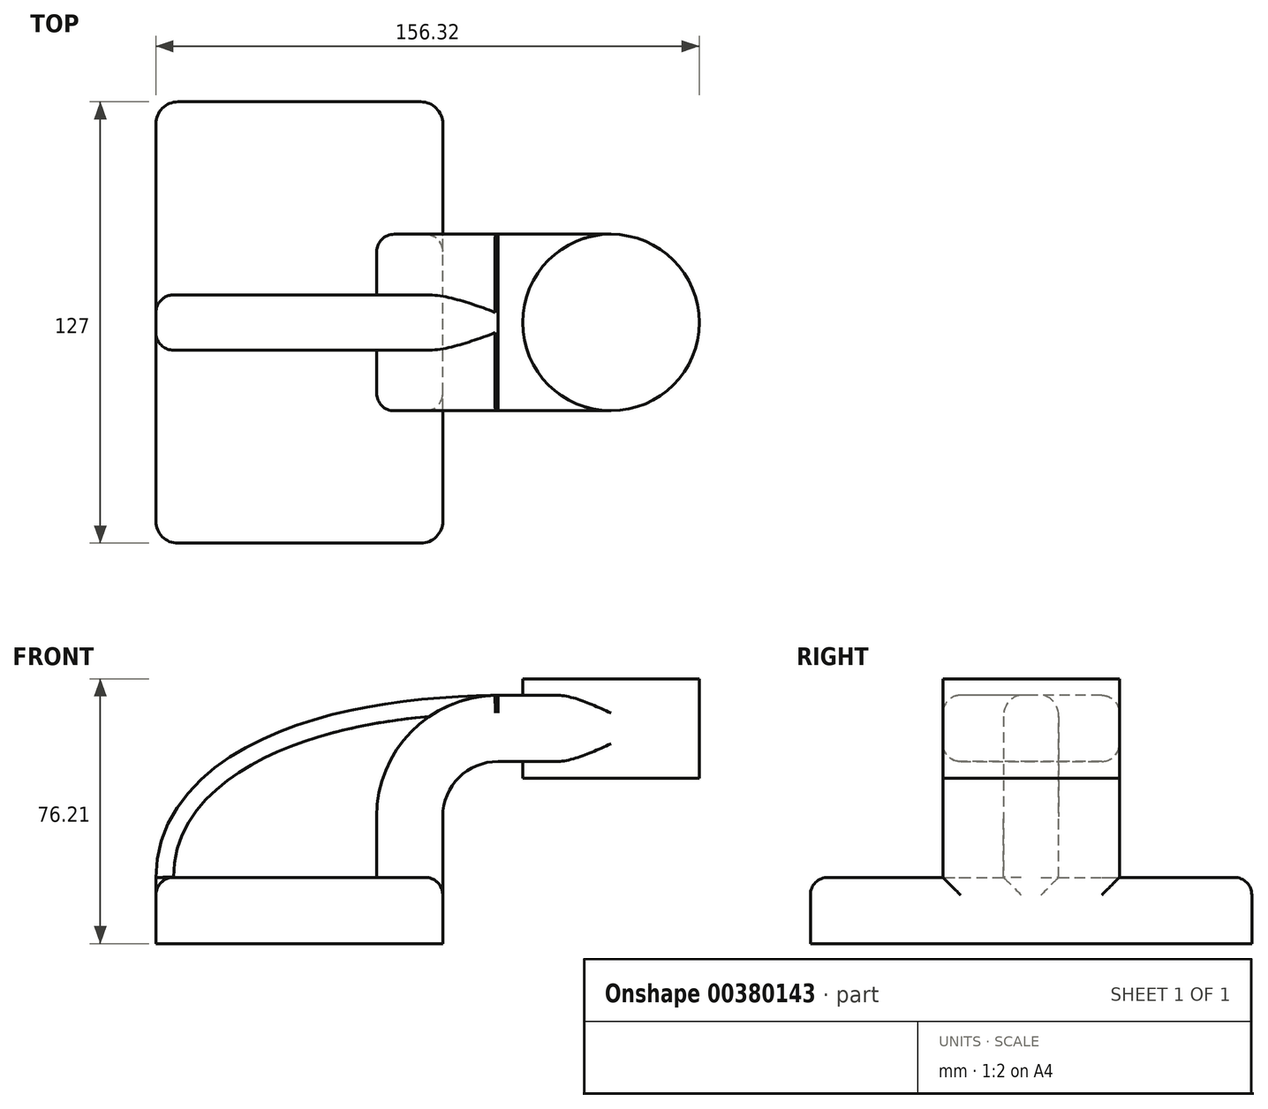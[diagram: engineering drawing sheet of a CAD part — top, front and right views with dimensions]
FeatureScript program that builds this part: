
annotation { "Feature Type Name" : "Feature", "Feature Type Description" : "" }
export const myFeature = defineFeature(function(context is Context, id is Id, definition is map)
    precondition{}
    {
        {
            var Q0;
            Q0=qCreatedBy(makeId("Front.planeOp"),FACE);
            var sketch = newSketch(context, id + "F0", { "sketchPlane" : qUnion([Q0])});
            skLineSegment(sketch, "E0.bottom", {"start": v(41.28, -9.52) * mm, "end": v(-41.28, -9.53) * mm});
            skLineSegment(sketch, "E0.top", {"start": v(41.27, 9.53) * mm, "end": v(-41.28, 9.53) * mm});
            skLineSegment(sketch, "E0.left", {"start": v(41.28, -9.52) * mm, "end": v(41.28, 9.53) * mm});
            skLineSegment(sketch, "E0.right", {"start": v(-41.28, -9.52) * mm, "end": v(-41.28, 9.53) * mm});
            skPoint(sketch, "E0.middle", {"position": v(0, 0) * mm});
            skLineSegment(sketch, "E1.bottom", {"start": v(115.04, 38.1) * mm, "end": v(64.24, 38.1) * mm});
            skLineSegment(sketch, "E1.top", {"start": v(115.04, 66.68) * mm, "end": v(64.24, 66.68) * mm});
            skLineSegment(sketch, "E1.left", {"start": v(115.04, 38.1) * mm, "end": v(115.04, 66.68) * mm});
            skLineSegment(sketch, "E1.right", {"start": v(64.24, 38.1) * mm, "end": v(64.24, 66.68) * mm});
            skPoint(sketch, "E1.middle", {"position": v(89.64, 52.39) * mm});
            skLineSegment(sketch, "E2", {"start": v(41.27, 9.53) * mm, "end": v(41.27, 27) * mm});
            skArc(sketch, "E3", {"start": v(41.27, 27) * mm, "mid": v(45.92, 38.23) * mm, "end": v(57.15, 42.88) * mm});
            skLineSegment(sketch, "E4", {"start": v(57.15, 42.88) * mm, "end": v(80.73, 42.88) * mm});
            skLineSegment(sketch, "E5.0", {"start": v(57.15, 61.93) * mm, "end": v(89.64, 61.93) * mm});
            skArc(sketch, "E5.1", {"start": v(22.23, 27) * mm, "mid": v(32.45, 51.7) * mm, "end": v(57.15, 61.93) * mm});
            skLineSegment(sketch, "E5.2", {"start": v(22.22, 9.53) * mm, "end": v(22.22, 27) * mm});
            skLineSegment(sketch, "E6", {"start": v(89.64, 38.1) * mm, "end": v(89.64, 66.68) * mm});
            skLineSegment(sketch, "E7", {"start": v(80.73, 42.88) * mm, "end": v(89.64, 42.88) * mm});
            skFitSpline(sketch, "E8", {"points": [v(-41.28, 9.53) * mm, v(57.15, 61.93) * mm], "startDerivative": vector(-0.8, 82.6) * mm, "endDerivative": vector(200.95, 2.16) * mm});
            skSolve(sketch);
        }
        {
            var Q0;
            Q0=makeQuery(id+"F0.imprint","IMPRINT",FACE,{"disambiguationData":[TD([[makeQuery(id+"F0.imprint","IMPRINT",EDGE,{"derivedFrom":sQuery(id+"F0.wireOp",EDGE,"E0.bottom")}),-1.0]])]});
            extrude(context, id + "F1", {"entities" : qUnion([Q0]), "endBound" : BoundingType.SYMMETRIC, "depth" : 127 * mm});
        }
        {
            var Q0;
            {var subQ1=sQuery(id+"F0.wireOp",EDGE,"E2");Q0=makeQuery(id+"F0.imprint","IMPRINT",FACE,{"disambiguationData":[TD([[makeQuery(id+"F0.imprint","IMPRINT",EDGE,{"derivedFrom":subQ1}),1.0]])]});}
            var Q1;
            {var subQ3=sQuery(id+"F0.wireOp",EDGE,"E7");Q1=makeQuery(id+"F0.imprint","IMPRINT",FACE,{"disambiguationData":[TD([[makeQuery(id+"F0.imprint","IMPRINT",EDGE,{"derivedFrom":subQ3}),1.0]])]});}
            extrude(context, id + "F2", {"entities" : qUnion([Q0, Q1]), "operationType" : NewBodyOperationType.ADD, "endBound" : BoundingType.SYMMETRIC, "depth" : 50.8 * mm});
        }
        {
            var Q0;
            {var subQ3=sQuery(id+"F0.wireOp",EDGE,"E5.2");Q0=makeQuery(id+"F0.imprint","IMPRINT",FACE,{"disambiguationData":[TD([[makeQuery(id+"F0.imprint","IMPRINT",EDGE,{"derivedFrom":subQ3}),1.0]])]});}
            extrude(context, id + "F3", {"entities" : qUnion([Q0]), "operationType" : NewBodyOperationType.ADD, "endBound" : BoundingType.SYMMETRIC, "depth" : 15.88 * mm});
        }
        {
            var Q0;
            {var subQ0=sQuery(id+"F0.wireOp",EDGE,"E1.left");Q0=makeQuery(id+"F0.imprint","IMPRINT",FACE,{"disambiguationData":[TD([[makeQuery(id+"F0.imprint","IMPRINT",EDGE,{"derivedFrom":subQ0}),1.0]])]});}
            var Q1;
            Q1=sQuery(id+"F0.wireOp",EDGE,"E6");
            revolve(context, id + "F4", {"operationType" : NewBodyOperationType.ADD, "entities" : qUnion([Q0]), "axis" : qUnion([Q1]), "revolveType" : RevolveType.FULL});
        }
        {
            var Q0;
            Q0=makeQuery(id+"F1.opExtrude","CAP_EDGE",EDGE,{"disambiguationData":[OSD([sQuery(id+"F0.wireOp",EDGE,"E0.left")])],"isStart":false});
            var Q1;
            Q1=makeQuery(id+"F1.opExtrude","CAP_EDGE",EDGE,{"disambiguationData":[OSD([sQuery(id+"F0.wireOp",EDGE,"E0.right")])],"isStart":false});
            var Q2;
            Q2=makeQuery(id+"F1.opExtrude","CAP_EDGE",EDGE,{"disambiguationData":[OSD([sQuery(id+"F0.wireOp",EDGE,"E0.left")])],"isStart":true});
            var Q3;
            Q3=makeQuery(id+"F1.opExtrude","CAP_EDGE",EDGE,{"disambiguationData":[OSD([sQuery(id+"F0.wireOp",EDGE,"E0.right")])],"isStart":true});
            fillet(context, id + "F5", {"entities" : qUnion([Q0, Q1, Q2, Q3]), "radius" : 6.35 * mm, "tangentPropagation" : true, "allowEdgeOverflow" : false});
        }
        {
            var Q0;
            Q0=makeQuery(id+"F3.opExtrude","CAP_EDGE",EDGE,{"disambiguationData":[OSD([sQuery(id+"F0.wireOp",EDGE,"E8")])],"isStart":true});
            var Q1;
            Q1=makeQuery(id+"F3.opExtrude","CAP_EDGE",EDGE,{"disambiguationData":[OSD([sQuery(id+"F0.wireOp",EDGE,"E8")])],"isStart":false});
            var Q2;
            Q2=makeQuery(id+"F2.opExtrude","CAP_EDGE",EDGE,{"disambiguationData":[OSD([sQuery(id+"F0.wireOp",EDGE,"E5.1")])],"isStart":true});
            var Q3;
            Q3=makeQuery(id+"F2.opExtrude","CAP_EDGE",EDGE,{"disambiguationData":[OSD([sQuery(id+"F0.wireOp",EDGE,"E5.2")])],"isStart":true});
            var Q4;
            Q4=makeQuery(id+"F2.opExtrude","CAP_EDGE",EDGE,{"disambiguationData":[OSD([sQuery(id+"F0.wireOp",EDGE,"E5.0")])],"isStart":true});
            var Q5;
            Q5=makeQuery(id+"F2.opExtrude","CAP_EDGE",EDGE,{"disambiguationData":[OSD([sQuery(id+"F0.wireOp",EDGE,"E5.0")])],"isStart":false});
            var Q6;
            Q6=makeQuery(id+"F2.opExtrude","CAP_EDGE",EDGE,{"disambiguationData":[OSD([sQuery(id+"F0.wireOp",EDGE,"E5.1")])],"isStart":false});
            var Q7;
            Q7=makeQuery(id+"F2.opExtrude","CAP_EDGE",EDGE,{"disambiguationData":[OSD([sQuery(id+"F0.wireOp",EDGE,"E5.2")])],"isStart":false});
            var Q8;
            Q8=makeQuery(id+"F2.opExtrude","CAP_EDGE",EDGE,{"disambiguationData":[OSD([sQuery(id+"F0.wireOp",EDGE,"E3")])],"isStart":true});
            var Q9;
            Q9=makeQuery(id+"F2.opExtrude","CAP_EDGE",EDGE,{"disambiguationData":[OSD([sQuery(id+"F0.wireOp",EDGE,"E4"),sQuery(id+"F0.wireOp",EDGE,"E7")])],"isStart":true});
            var Q10;
            Q10=makeQuery(id+"F2.opExtrude","CAP_EDGE",EDGE,{"disambiguationData":[OSD([sQuery(id+"F0.wireOp",EDGE,"E2")])],"isStart":true});
            var Q11;
            Q11=makeQuery(id+"F2.opExtrude","CAP_EDGE",EDGE,{"disambiguationData":[OSD([sQuery(id+"F0.wireOp",EDGE,"E2")])],"isStart":false});
            var Q12;
            Q12=makeQuery(id+"F2.opExtrude","CAP_EDGE",EDGE,{"disambiguationData":[OSD([sQuery(id+"F0.wireOp",EDGE,"E4"),sQuery(id+"F0.wireOp",EDGE,"E7")])],"isStart":false});
            var Q13;
            Q13=makeQuery(id+"F2.opExtrude","CAP_EDGE",EDGE,{"disambiguationData":[OSD([sQuery(id+"F0.wireOp",EDGE,"E3")])],"isStart":false});
            var Q14;
            Q14=makeQuery(id+"F1.opExtrude","CAP_EDGE",EDGE,{"disambiguationData":[OSD([sQuery(id+"F0.wireOp",EDGE,"E0.top")])],"isStart":true});
            var Q15;
            {var subQ4=sQuery(id+"F0.wireOp",EDGE,"E0.top");var subQ5=sQuery(id+"F0.wireOp",EDGE,"E0.right");var subQ6=sQuery(id+"F0.wireOp",EDGE,"E0.left");Q15=makeQuery(id+"F5.opFillet","BLEND_EDGE",EDGE,{"blendedFrom":[makeQuery(id+"F1.opExtrude","CAP_EDGE",EDGE,{"disambiguationData":[OSD([subQ5])],"isStart":true}),makeQuery(id+"F3.boolean.opBoolean","SPLIT",FACE,{"disambiguationData":[TD([makeQuery(id+"F1.opExtrude","CAP_FACE",FACE,{"disambiguationData":[OSD([sQuery(id+"F0.wireOp",EDGE,"E0.bottom"),subQ4,subQ6,subQ5])],"isStart":true})])],"derivedFrom":makeQuery(id+"F1.opExtrude","SWEPT_FACE",FACE,{"disambiguationData":[OSD([subQ4])]})})],"blendedInto":[makeQuery(id+"F3.boolean.opBoolean","SPLIT",FACE,{"disambiguationData":[TD([makeQuery(id+"F1.opExtrude","CAP_FACE",FACE,{"disambiguationData":[OSD([sQuery(id+"F0.wireOp",EDGE,"E0.bottom"),subQ4,subQ6,subQ5])],"isStart":true})])],"derivedFrom":makeQuery(id+"F1.opExtrude","SWEPT_FACE",FACE,{"disambiguationData":[OSD([subQ4])]})})]});}
            var Q16;
            {var subQ0=sQuery(id+"F0.wireOp",EDGE,"E0.right");var subQ1=sQuery(id+"F0.wireOp",EDGE,"E0.top");var subQ2=sQuery(id+"F0.wireOp",EDGE,"E8");Q16=makeQuery(id+"F3.boolean.opBoolean","SPLIT",EDGE,{"disambiguationData":[TD([makeQuery(id+"F1.opExtrude","CAP_FACE",FACE,{"disambiguationData":[OSD([sQuery(id+"F0.wireOp",EDGE,"E0.bottom"),subQ1,sQuery(id+"F0.wireOp",EDGE,"E0.left"),subQ0])],"isStart":true})])],"derivedFrom":makeQuery(id+"F1.opExtrude","SWEPT_EDGE",EDGE,{"disambiguationData":[OSD([subQ1,subQ0,subQ2])]})});}
            var Q17;
            {var subQ0=sQuery(id+"F0.wireOp",EDGE,"E8");var subQ1=sQuery(id+"F0.wireOp",EDGE,"E0.top");var subQ2=sQuery(id+"F0.wireOp",EDGE,"E0.right");Q17=makeQuery(id+"F3.boolean.opBoolean","SPLIT",EDGE,{"disambiguationData":[TD([makeQuery(id+"F1.opExtrude","CAP_FACE",FACE,{"disambiguationData":[OSD([sQuery(id+"F0.wireOp",EDGE,"E0.bottom"),subQ1,sQuery(id+"F0.wireOp",EDGE,"E0.left"),subQ2])],"isStart":false})])],"derivedFrom":makeQuery(id+"F1.opExtrude","SWEPT_EDGE",EDGE,{"disambiguationData":[OSD([subQ1,subQ2,subQ0])]})});}
            var Q18;
            Q18=makeQuery(id+"F1.opExtrude","CAP_EDGE",EDGE,{"disambiguationData":[OSD([sQuery(id+"F0.wireOp",EDGE,"E0.top")])],"isStart":false});
            var Q19;
            {var subQ4=sQuery(id+"F0.wireOp",EDGE,"E0.top");var subQ5=sQuery(id+"F0.wireOp",EDGE,"E0.right");var subQ6=sQuery(id+"F0.wireOp",EDGE,"E0.left");Q19=makeQuery(id+"F5.opFillet","BLEND_EDGE",EDGE,{"blendedFrom":[makeQuery(id+"F1.opExtrude","CAP_EDGE",EDGE,{"disambiguationData":[OSD([subQ5])],"isStart":false}),makeQuery(id+"F3.boolean.opBoolean","SPLIT",FACE,{"disambiguationData":[TD([makeQuery(id+"F1.opExtrude","CAP_FACE",FACE,{"disambiguationData":[OSD([sQuery(id+"F0.wireOp",EDGE,"E0.bottom"),subQ4,subQ6,subQ5])],"isStart":false})])],"derivedFrom":makeQuery(id+"F1.opExtrude","SWEPT_FACE",FACE,{"disambiguationData":[OSD([subQ4])]})})],"blendedInto":[makeQuery(id+"F3.boolean.opBoolean","SPLIT",FACE,{"disambiguationData":[TD([makeQuery(id+"F1.opExtrude","CAP_FACE",FACE,{"disambiguationData":[OSD([sQuery(id+"F0.wireOp",EDGE,"E0.bottom"),subQ4,subQ6,subQ5])],"isStart":false})])],"derivedFrom":makeQuery(id+"F1.opExtrude","SWEPT_FACE",FACE,{"disambiguationData":[OSD([subQ4])]})})]});}
            var Q20;
            {var subQ4=sQuery(id+"F0.wireOp",EDGE,"E0.top");var subQ5=sQuery(id+"F0.wireOp",EDGE,"E0.right");var subQ6=sQuery(id+"F0.wireOp",EDGE,"E0.left");Q20=makeQuery(id+"F5.opFillet","BLEND_EDGE",EDGE,{"blendedFrom":[makeQuery(id+"F1.opExtrude","CAP_EDGE",EDGE,{"disambiguationData":[OSD([subQ6])],"isStart":false}),makeQuery(id+"F3.boolean.opBoolean","SPLIT",FACE,{"disambiguationData":[TD([makeQuery(id+"F1.opExtrude","CAP_FACE",FACE,{"disambiguationData":[OSD([sQuery(id+"F0.wireOp",EDGE,"E0.bottom"),subQ4,subQ6,subQ5])],"isStart":false})])],"derivedFrom":makeQuery(id+"F1.opExtrude","SWEPT_FACE",FACE,{"disambiguationData":[OSD([subQ4])]})})],"blendedInto":[makeQuery(id+"F3.boolean.opBoolean","SPLIT",FACE,{"disambiguationData":[TD([makeQuery(id+"F1.opExtrude","CAP_FACE",FACE,{"disambiguationData":[OSD([sQuery(id+"F0.wireOp",EDGE,"E0.bottom"),subQ4,subQ6,subQ5])],"isStart":false})])],"derivedFrom":makeQuery(id+"F1.opExtrude","SWEPT_FACE",FACE,{"disambiguationData":[OSD([subQ4])]})})]});}
            var Q21;
            {var subQ0=sQuery(id+"F0.wireOp",EDGE,"E0.left");var subQ1=sQuery(id+"F0.wireOp",EDGE,"E2");var subQ2=sQuery(id+"F0.wireOp",EDGE,"E0.top");Q21=makeQuery(id+"F2.boolean.opBoolean","SPLIT",EDGE,{"disambiguationData":[TD([makeQuery(id+"F1.opExtrude","CAP_FACE",FACE,{"disambiguationData":[OSD([sQuery(id+"F0.wireOp",EDGE,"E0.bottom"),subQ2,subQ0,sQuery(id+"F0.wireOp",EDGE,"E0.right")])],"isStart":false})])],"derivedFrom":makeQuery(id+"F1.opExtrude","SWEPT_EDGE",EDGE,{"disambiguationData":[OSD([subQ2,subQ0,subQ1])]})});}
            var Q22;
            {var subQ0=sQuery(id+"F0.wireOp",EDGE,"E2");var subQ1=sQuery(id+"F0.wireOp",EDGE,"E0.top");var subQ2=sQuery(id+"F0.wireOp",EDGE,"E0.left");Q22=makeQuery(id+"F2.boolean.opBoolean","SPLIT",EDGE,{"disambiguationData":[TD([makeQuery(id+"F1.opExtrude","CAP_FACE",FACE,{"disambiguationData":[OSD([sQuery(id+"F0.wireOp",EDGE,"E0.bottom"),subQ1,subQ2,sQuery(id+"F0.wireOp",EDGE,"E0.right")])],"isStart":true})])],"derivedFrom":makeQuery(id+"F1.opExtrude","SWEPT_EDGE",EDGE,{"disambiguationData":[OSD([subQ1,subQ2,subQ0])]})});}
            var Q23;
            {var subQ4=sQuery(id+"F0.wireOp",EDGE,"E0.top");var subQ5=sQuery(id+"F0.wireOp",EDGE,"E0.right");var subQ6=sQuery(id+"F0.wireOp",EDGE,"E0.left");Q23=makeQuery(id+"F5.opFillet","BLEND_EDGE",EDGE,{"blendedFrom":[makeQuery(id+"F1.opExtrude","CAP_EDGE",EDGE,{"disambiguationData":[OSD([subQ6])],"isStart":true}),makeQuery(id+"F3.boolean.opBoolean","SPLIT",FACE,{"disambiguationData":[TD([makeQuery(id+"F1.opExtrude","CAP_FACE",FACE,{"disambiguationData":[OSD([sQuery(id+"F0.wireOp",EDGE,"E0.bottom"),subQ4,subQ6,subQ5])],"isStart":true})])],"derivedFrom":makeQuery(id+"F1.opExtrude","SWEPT_FACE",FACE,{"disambiguationData":[OSD([subQ4])]})})],"blendedInto":[makeQuery(id+"F3.boolean.opBoolean","SPLIT",FACE,{"disambiguationData":[TD([makeQuery(id+"F1.opExtrude","CAP_FACE",FACE,{"disambiguationData":[OSD([sQuery(id+"F0.wireOp",EDGE,"E0.bottom"),subQ4,subQ6,subQ5])],"isStart":true})])],"derivedFrom":makeQuery(id+"F1.opExtrude","SWEPT_FACE",FACE,{"disambiguationData":[OSD([subQ4])]})})]});}
            fillet(context, id + "F6", {"entities" : qUnion([Q0, Q1, Q2, Q3, Q4, Q5, Q6, Q7, Q8, Q9, Q10, Q11, Q12, Q13, Q14, Q15, Q16, Q17, Q18, Q19, Q20, Q21, Q22, Q23]), "radius" : 5.08 * mm, "tangentPropagation" : true, "allowEdgeOverflow" : false});
        }
    });
